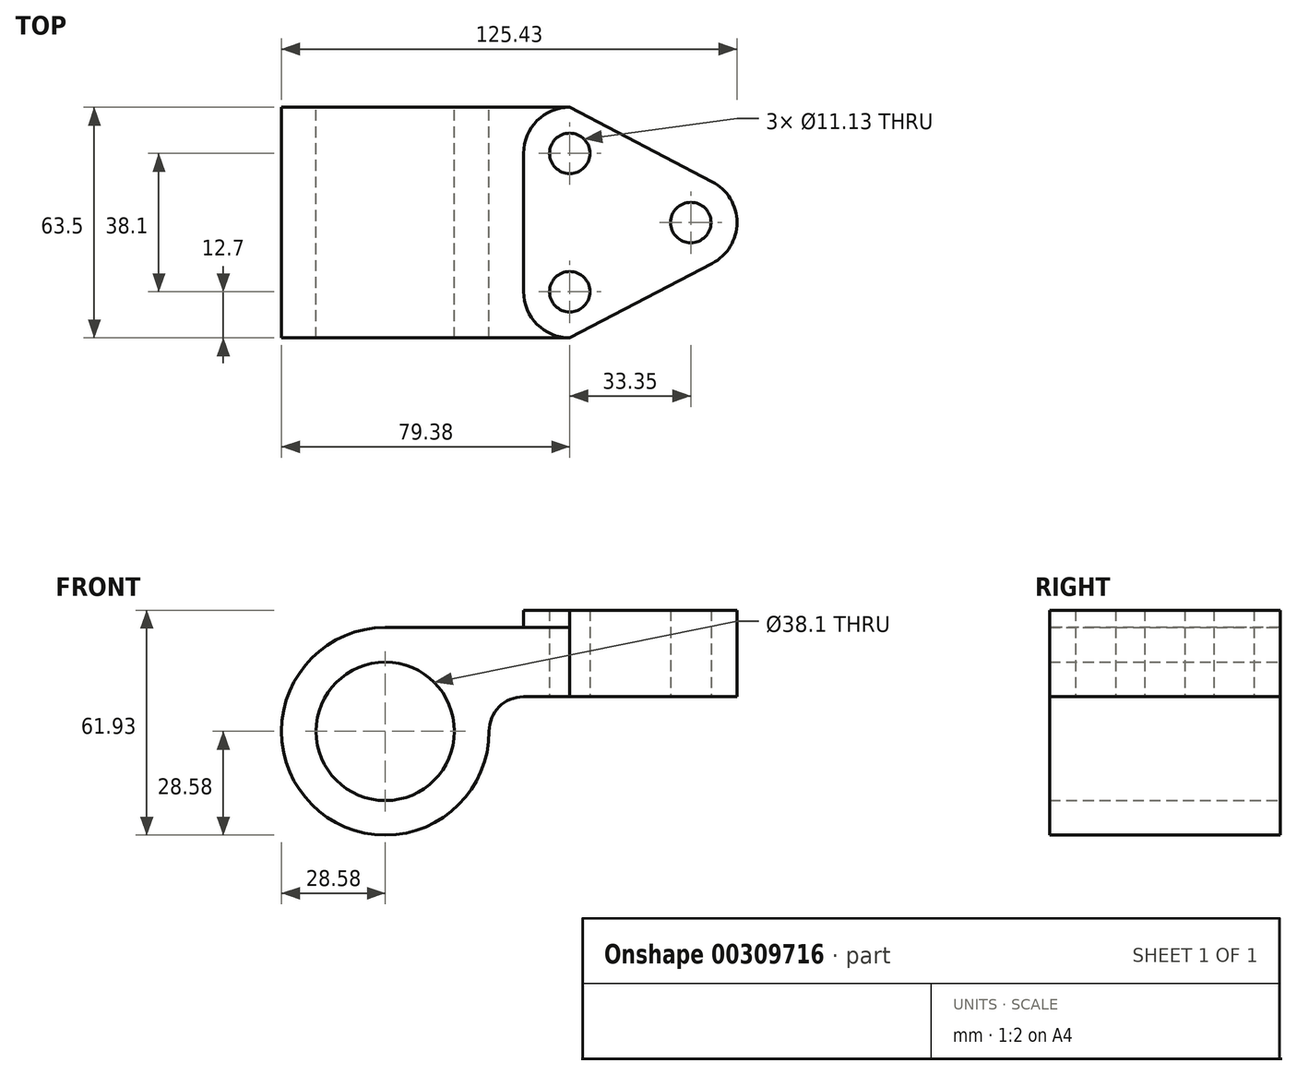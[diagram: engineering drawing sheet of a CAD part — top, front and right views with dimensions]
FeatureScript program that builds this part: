
annotation { "Feature Type Name" : "Feature", "Feature Type Description" : "" }
export const myFeature = defineFeature(function(context is Context, id is Id, definition is map)
    precondition{}
    {
        {
            var Q0;
            Q0=qCreatedBy(makeId("Front.planeOp"),FACE);
            var sketch = newSketch(context, id + "F0", { "sketchPlane" : qUnion([Q0])});
            skCircle(sketch, "E0", {"center": v(0, 0) * mm, "radius": 19.05 * mm});
            skArc(sketch, "E1", {"start": v(0, 28.58) * mm, "mid": v(-20.2, -20.2) * mm, "end": v(28.58, 0) * mm});
            skLineSegment(sketch, "E2", {"start": v(0, 28.58) * mm, "end": v(50.8, 28.58) * mm});
            skArc(sketch, "E3", {"start": v(28.58, 0) * mm, "mid": v(31.36, 6.74) * mm, "end": v(38.1, 9.53) * mm});
            skLineSegment(sketch, "E4", {"start": v(50.8, 28.58) * mm, "end": v(50.8, 9.53) * mm});
            skLineSegment(sketch, "E5", {"start": v(50.8, 9.53) * mm, "end": v(38.1, 9.53) * mm});
            skSolve(sketch);
        }
        {
            var Q0;
            Q0=makeQuery(id+"F0.imprint","IMPRINT",FACE,{"disambiguationData":[TD([[makeQuery(id+"F0.imprint","IMPRINT",EDGE,{"derivedFrom":sQuery(id+"F0.wireOp",EDGE,"E0")}),-1.0]])]});
            extrude(context, id + "F1", {"entities" : qUnion([Q0]), "endBound" : BoundingType.SYMMETRIC, "depth" : 63.5 * mm});
        }
        {
            var Q0;
            Q0=makeQuery(id+"F1.opExtrude","SWEPT_FACE",FACE,{"disambiguationData":[OSD([sQuery(id+"F0.wireOp",EDGE,"E2")])]});
            var sketch = newSketch(context, id + "F2", { "sketchPlane" : qUnion([Q0])});
            skPoint(sketch, "E6.endSnap0", {"position": v(25.4, -31.75) * mm});
            skLineSegment(sketch, "E7", {"start": v(50.8, 41.83) * mm, "end": v(50.8, -44.41) * mm, "construction": true});
            skLineSegment(sketch, "E8", {"start": v(0, 0) * mm, "end": v(126.68, 0) * mm, "construction": true});
            skPoint(sketch, "E8.endSnap0", {"position": v(50.8, 0) * mm});
            skCircle(sketch, "E9", {"center": v(50.8, 19.05) * mm, "radius": 5.56 * mm});
            skCircle(sketch, "E10", {"center": v(50.8, -19.05) * mm, "radius": 5.56 * mm});
            skCircle(sketch, "E11", {"center": v(84.15, 0) * mm, "radius": 5.56 * mm});
            skLineSegment(sketch, "E12", {"start": v(38.1, 19.05) * mm, "end": v(38.1, -19.05) * mm});
            skArc(sketch, "E13", {"start": v(38.1, 19.05) * mm, "mid": v(41.82, 28.03) * mm, "end": v(50.8, 31.75) * mm});
            skArc(sketch, "E14", {"start": v(38.1, -19.05) * mm, "mid": v(41.82, -28.03) * mm, "end": v(50.8, -31.75) * mm});
            skLineSegment(sketch, "E15", {"start": v(50.8, 31.75) * mm, "end": v(90.03, 11.26) * mm});
            skLineSegment(sketch, "E16", {"start": v(50.8, -31.75) * mm, "end": v(90.03, -11.26) * mm});
            skArc(sketch, "E17", {"start": v(90.03, 11.26) * mm, "mid": v(96.85, 0) * mm, "end": v(90.03, -11.26) * mm});
            skSolve(sketch);
        }
        {
            var Q0;
            Q0 = qSketchRegion(id + "F2", true);
            extrude(context, id + "F3", {"entities" : qUnion([Q0]), "operationType" : NewBodyOperationType.ADD, "depth" : 4.78 * mm});
        }
        {
            var Q0;
            Q0=makeQuery(id+"F3.opExtrude","CAP_FACE",FACE,{"disambiguationData":[OSD([sQuery(id+"F2.wireOp",EDGE,"E9"),sQuery(id+"F2.wireOp",EDGE,"E10"),sQuery(id+"F2.wireOp",EDGE,"E11"),sQuery(id+"F2.wireOp",EDGE,"E12"),sQuery(id+"F2.wireOp",EDGE,"E13"),sQuery(id+"F2.wireOp",EDGE,"E14"),sQuery(id+"F2.wireOp",EDGE,"E15"),sQuery(id+"F2.wireOp",EDGE,"E16"),sQuery(id+"F2.wireOp",EDGE,"E17")])],"isStart":true});
            var Q1;
            Q1=makeQuery(id+"F1.opExtrude","CAP_VERTEX",VERTEX,{"disambiguationData":[OSD([sQuery(id+"F0.wireOp",EDGE,"E4"),sQuery(id+"F0.wireOp",EDGE,"E5")])],"isStart":true});
            extrude(context, id + "F4", {"entities" : qUnion([Q0]), "operationType" : NewBodyOperationType.ADD, "endBound" : BoundingType.UP_TO_VERTEX, "endBoundEntityVertex" : qUnion([Q1]), "depth" : 15.88 * mm});
        }
        {
            var Q0;
            {var subQ0=sQuery(id+"F2.wireOp",EDGE,"E9");Q0=makeQuery(id+"F3.boolean.opBoolean","SPLIT",FACE,{"disambiguationData":[TD([makeQuery(id+"F3.opExtrude","SWEPT_FACE",FACE,{"disambiguationData":[OSD([subQ0])]})])],"derivedFrom":makeQuery(id+"F1.opExtrude","SWEPT_FACE",FACE,{"disambiguationData":[OSD([sQuery(id+"F0.wireOp",EDGE,"E2")])]})});}
            var Q1;
            {var subQ0=sQuery(id+"F2.wireOp",EDGE,"E10");Q1=makeQuery(id+"F3.boolean.opBoolean","SPLIT",FACE,{"disambiguationData":[TD([makeQuery(id+"F3.opExtrude","SWEPT_FACE",FACE,{"disambiguationData":[OSD([subQ0])]})])],"derivedFrom":makeQuery(id+"F1.opExtrude","SWEPT_FACE",FACE,{"disambiguationData":[OSD([sQuery(id+"F0.wireOp",EDGE,"E2")])]})});}
            extrude(context, id + "F5", {"entities" : qUnion([Q0, Q1]), "operationType" : NewBodyOperationType.REMOVE, "oppositeDirection" : true, "depth" : 25.4 * mm});
        }
    });
